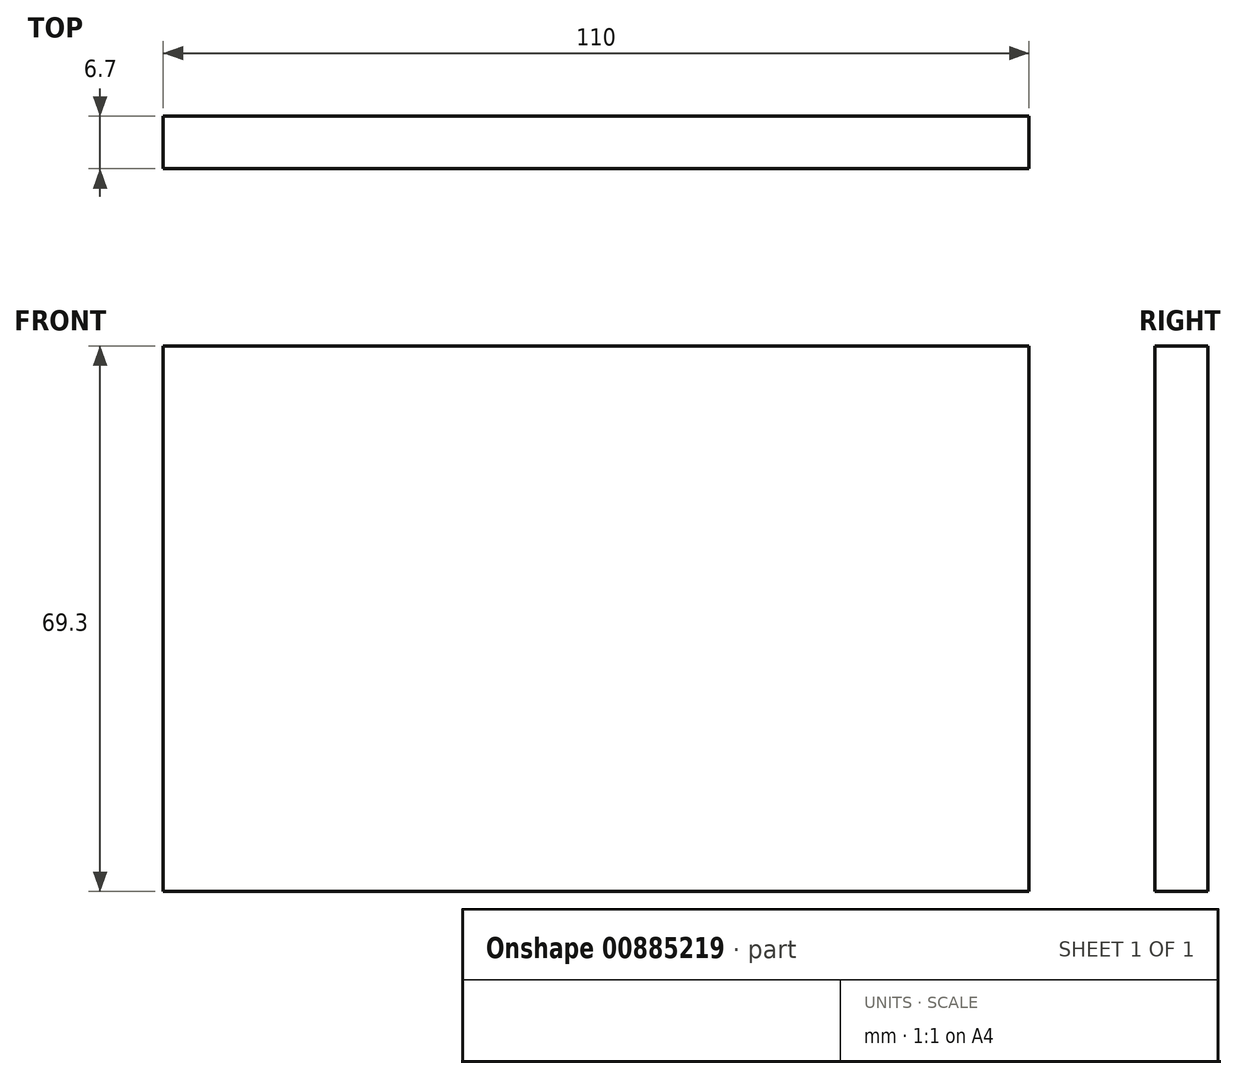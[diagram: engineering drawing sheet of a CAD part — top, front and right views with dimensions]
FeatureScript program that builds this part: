
annotation { "Feature Type Name" : "Feature", "Feature Type Description" : "" }
export const myFeature = defineFeature(function(context is Context, id is Id, definition is map)
    precondition{}
    {
        {
            var Q0;
            Q0=qCreatedBy(makeId("Front.planeOp"),FACE);
            var sketch = newSketch(context, id + "F0", { "sketchPlane" : qUnion([Q0])});
            skLineSegment(sketch, "E0.bottom", {"start": v(-57.46, 69.3) * mm, "end": v(52.54, 69.3) * mm});
            skLineSegment(sketch, "E0.top", {"start": v(-57.46, 0) * mm, "end": v(52.54, 0) * mm});
            skLineSegment(sketch, "E0.left", {"start": v(-57.46, 69.3) * mm, "end": v(-57.46, 0) * mm});
            skLineSegment(sketch, "E0.right", {"start": v(52.54, 69.3) * mm, "end": v(52.54, 0) * mm});
            skSolve(sketch);
        }
        {
            var Q0;
            Q0=makeQuery(id+"F0.imprint","IMPRINT",FACE,{"disambiguationData":[TD([[makeQuery(id+"F0.imprint","IMPRINT",EDGE,{"derivedFrom":sQuery(id+"F0.wireOp",EDGE,"E0.bottom")}),-1.0]])]});
            extrude(context, id + "F1", {"entities" : qUnion([Q0]), "depth" : 6.7 * mm, "offsetDistance" : 25 * mm});
        }
    });
